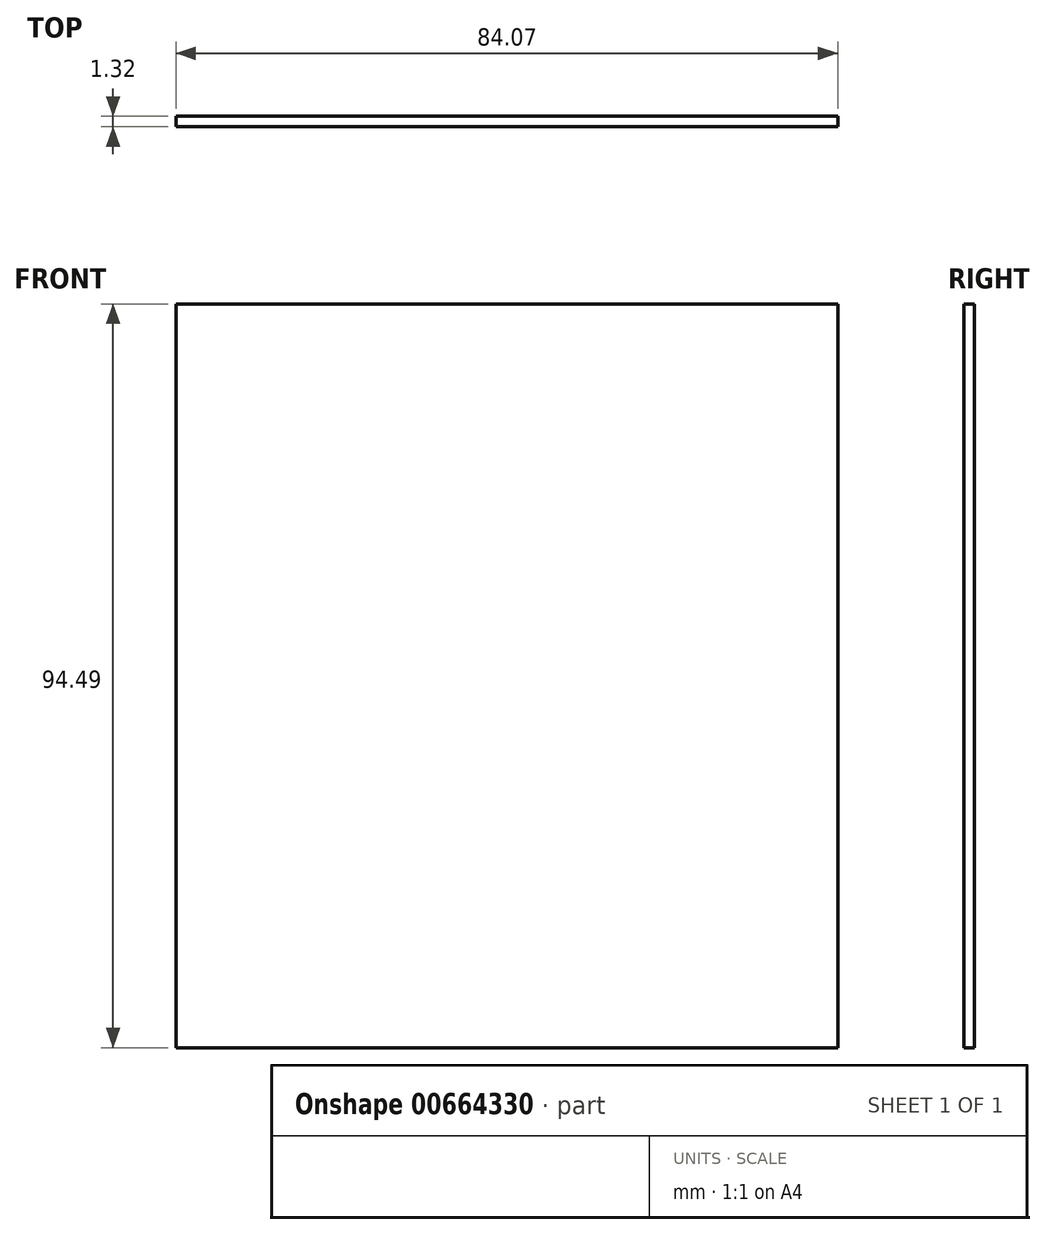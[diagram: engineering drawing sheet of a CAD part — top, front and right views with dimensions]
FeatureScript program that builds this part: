
annotation { "Feature Type Name" : "Feature", "Feature Type Description" : "" }
export const myFeature = defineFeature(function(context is Context, id is Id, definition is map)
    precondition{}
    {
        {
            var Q0;
            Q0=qCreatedBy(makeId("Front.planeOp"),FACE);
            var sketch = newSketch(context, id + "F0", { "sketchPlane" : qUnion([Q0])});
            skLineSegment(sketch, "E0.bottom", {"start": v(0, 0) * mm, "end": v(84.07, 0) * mm});
            skLineSegment(sketch, "E0.top", {"start": v(0, 94.49) * mm, "end": v(84.07, 94.49) * mm});
            skLineSegment(sketch, "E0.left", {"start": v(0, 0) * mm, "end": v(0, 94.49) * mm});
            skLineSegment(sketch, "E0.right", {"start": v(84.07, 0) * mm, "end": v(84.07, 94.49) * mm});
            skSolve(sketch);
        }
        {
            var Q0;
            Q0=makeQuery(id+"F0.imprint","IMPRINT",FACE,{"disambiguationData":[TD([[makeQuery(id+"F0.imprint","IMPRINT",EDGE,{"derivedFrom":sQuery(id+"F0.wireOp",EDGE,"E0.bottom")}),1.0]])]});
            extrude(context, id + "F1", {"entities" : qUnion([Q0]), "depth" : 1.32 * mm, "offsetDistance" : 25.4 * mm});
        }
    });
